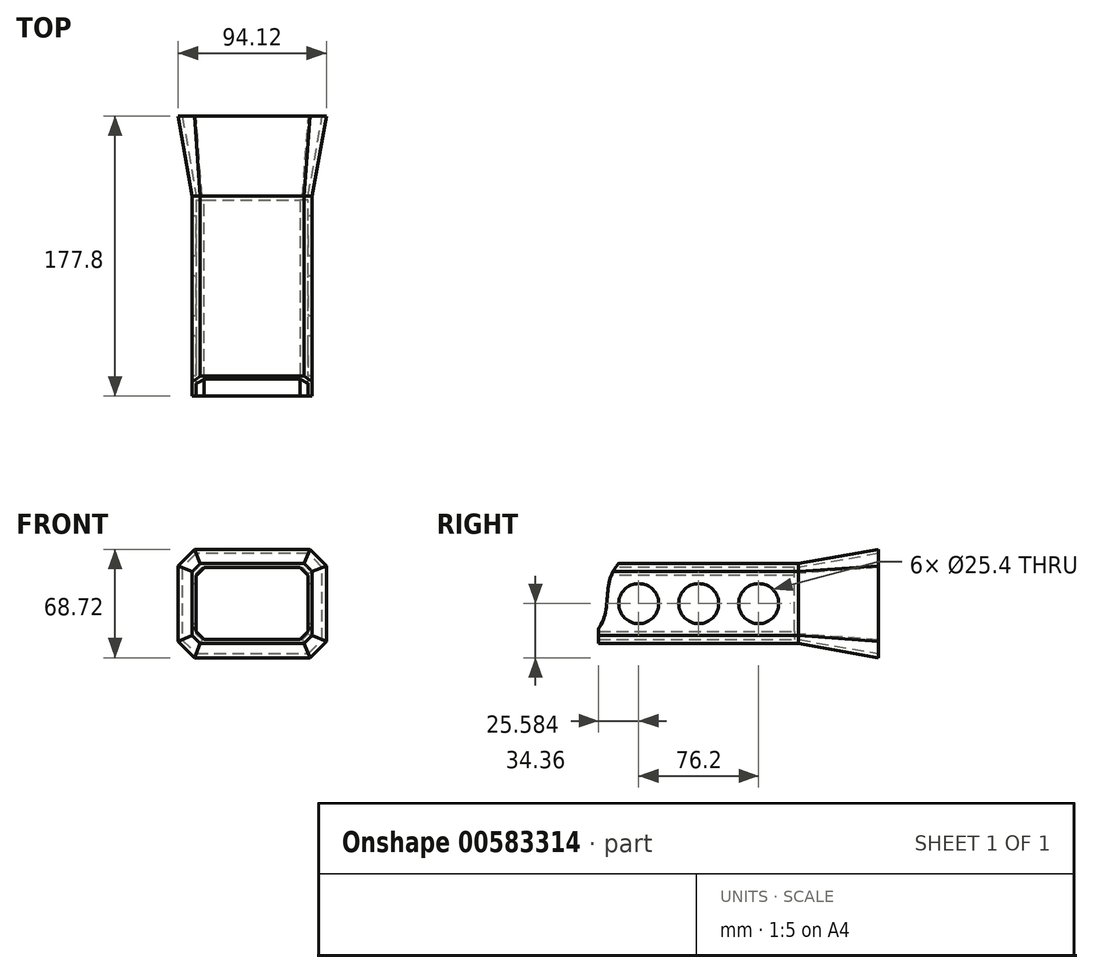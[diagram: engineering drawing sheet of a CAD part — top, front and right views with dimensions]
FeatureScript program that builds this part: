
annotation { "Feature Type Name" : "Feature", "Feature Type Description" : "" }
export const myFeature = defineFeature(function(context is Context, id is Id, definition is map)
    precondition{}
    {
        {
            var Q0;
            Q0=qCreatedBy(makeId("Front.planeOp"),FACE);
            var sketch = newSketch(context, id + "F0", { "sketchPlane" : qUnion([Q0])});
            skLineSegment(sketch, "E0.bottom", {"start": v(0, 0) * mm, "end": v(76.2, 0) * mm});
            skLineSegment(sketch, "E0.top", {"start": v(0, 50.8) * mm, "end": v(76.2, 50.8) * mm});
            skLineSegment(sketch, "E0.left", {"start": v(0, 0) * mm, "end": v(0, 50.8) * mm});
            skLineSegment(sketch, "E0.right", {"start": v(76.2, 0) * mm, "end": v(76.2, 50.8) * mm});
            skSolve(sketch);
        }
        {
            var Q0;
            Q0 = qSketchRegion(id + "F0", true);
            extrude(context, id + "F1", {"entities" : qUnion([Q0]), "depth" : 127 * mm, "offsetDistance" : 25.4 * mm});
        }
        {
            var Q0;
            Q0=makeQuery(id+"F1.opExtrude","CAP_FACE",FACE,{"disambiguationData":[OSD([sQuery(id+"F0.wireOp",EDGE,"E0.bottom"),sQuery(id+"F0.wireOp",EDGE,"E0.top"),sQuery(id+"F0.wireOp",EDGE,"E0.left"),sQuery(id+"F0.wireOp",EDGE,"E0.right")])],"isStart":false});
            shell(context, id + "F2", {"entities" : qUnion([Q0]), "thickness" : 2.54 * mm});
        }
        {
            var Q0;
            Q0=makeQuery(id+"F1.opExtrude","SWEPT_FACE",FACE,{"disambiguationData":[OSD([sQuery(id+"F0.wireOp",EDGE,"E0.right")])]});
            var sketch = newSketch(context, id + "F3", { "sketchPlane" : qUnion([Q0])});
            skCircle(sketch, "E1", {"center": v(-101.42, 25.4) * mm, "radius": 12.7 * mm});
            skCircle(sketch, "E2", {"center": v(-63.32, 25.4) * mm, "radius": 12.7 * mm});
            skCircle(sketch, "E3", {"center": v(-25.22, 25.4) * mm, "radius": 12.7 * mm});
            skSolve(sketch);
        }
        {
            var Q0;
            Q0=makeQuery(id+"F3.imprint","IMPRINT",FACE,{"disambiguationData":[TD([[makeQuery(id+"F3.imprint","IMPRINT",EDGE,{"derivedFrom":sQuery(id+"F3.wireOp",EDGE,"E1")}),1.0]])]});
            var Q1;
            Q1=makeQuery(id+"F3.imprint","IMPRINT",FACE,{"disambiguationData":[TD([[makeQuery(id+"F3.imprint","IMPRINT",EDGE,{"derivedFrom":sQuery(id+"F3.wireOp",EDGE,"E2")}),1.0]])]});
            var Q2;
            Q2=makeQuery(id+"F3.imprint","IMPRINT",FACE,{"disambiguationData":[TD([[makeQuery(id+"F3.imprint","IMPRINT",EDGE,{"derivedFrom":sQuery(id+"F3.wireOp",EDGE,"E3")}),1.0]])]});
            extrude(context, id + "F4", {"entities" : qUnion([Q0, Q1, Q2]), "operationType" : NewBodyOperationType.REMOVE, "endBound" : BoundingType.THROUGH_ALL, "oppositeDirection" : true, "depth" : 25.4 * mm, "offsetDistance" : 25.4 * mm});
        }
        {
            var Q0;
            Q0=makeQuery(id+"F1.opExtrude","SWEPT_FACE",FACE,{"disambiguationData":[OSD([sQuery(id+"F0.wireOp",EDGE,"E0.right")])]});
            var sketch = newSketch(context, id + "F5", { "sketchPlane" : qUnion([Q0])});
            skFitSpline(sketch, "E4", {"points": [v(-105.13, 60.93) * mm, v(-119.3, 42.33) * mm, v(-123.68, 15.71) * mm, v(-145.7, -4.89) * mm], "startDerivative": vector(-47.95, -55.16) * mm, "endDerivative": vector(-90.34, -45.67) * mm});
            skSolve(sketch);
        }
        {
            var Q0;
            Q0 = qSketchRegion(id + "F5", true);
            var Q1;
            {var subQ0=sQuery(id+"F5.wireOp",EDGE,"E4");var subQ1=sQuery(id+"F0.wireOp",EDGE,"E0.right");var subQ4=makeQuery(id+"F1.opExtrude","CAP_EDGE",EDGE,{"disambiguationData":[OSD([subQ1])],"isStart":false});var subQ5=makeQuery(id+"F5.imprint","INTERSECT",VERTEX,{"derivedFrom":[subQ4,subQ0]});Q1=makeQuery(id+"F5.imprint","IMPRINT",FACE,{"disambiguationData":[TD([[makeQuery(id+"F5.imprint","IMPRINT",EDGE,{"disambiguationData":[TD([[subQ5,1.0]])],"derivedFrom":subQ0}),-1.0]])]});}
            extrude(context, id + "F6", {"entities" : qUnion([Q0, Q1]), "operationType" : NewBodyOperationType.REMOVE, "endBound" : BoundingType.THROUGH_ALL, "oppositeDirection" : true, "depth" : 25.4 * mm, "offsetDistance" : 25.4 * mm});
        }
        {
            var Q0;
            Q0=makeQuery(id+"F2.opShell","OFFSET_EDGE",EDGE,{"disambiguationData":[OSD([sQuery(id+"F0.wireOp",EDGE,"E0.bottom"),sQuery(id+"F0.wireOp",EDGE,"E0.left")])]});
            var Q1;
            Q1=makeQuery(id+"F2.opShell","OFFSET_EDGE",EDGE,{"disambiguationData":[OSD([sQuery(id+"F0.wireOp",EDGE,"E0.bottom"),sQuery(id+"F0.wireOp",EDGE,"E0.right")])]});
            var Q2;
            Q2=makeQuery(id+"F2.opShell","OFFSET_EDGE",EDGE,{"disambiguationData":[OSD([sQuery(id+"F0.wireOp",EDGE,"E0.top"),sQuery(id+"F0.wireOp",EDGE,"E0.left")])]});
            var Q3;
            Q3=makeQuery(id+"F2.opShell","OFFSET_EDGE",EDGE,{"disambiguationData":[OSD([sQuery(id+"F0.wireOp",EDGE,"E0.top"),sQuery(id+"F0.wireOp",EDGE,"E0.right")])]});
            var Q4;
            Q4=makeQuery(id+"F1.opExtrude","SWEPT_EDGE",EDGE,{"disambiguationData":[OSD([sQuery(id+"F0.wireOp",EDGE,"E0.top"),sQuery(id+"F0.wireOp",EDGE,"E0.left")])]});
            var Q5;
            Q5=makeQuery(id+"F1.opExtrude","SWEPT_EDGE",EDGE,{"disambiguationData":[OSD([sQuery(id+"F0.wireOp",EDGE,"E0.top"),sQuery(id+"F0.wireOp",EDGE,"E0.right")])]});
            var Q6;
            Q6=makeQuery(id+"F1.opExtrude","SWEPT_EDGE",EDGE,{"disambiguationData":[OSD([sQuery(id+"F0.wireOp",EDGE,"E0.bottom"),sQuery(id+"F0.wireOp",EDGE,"E0.left")])]});
            var Q7;
            Q7=makeQuery(id+"F1.opExtrude","SWEPT_EDGE",EDGE,{"disambiguationData":[OSD([sQuery(id+"F0.wireOp",EDGE,"E0.bottom"),sQuery(id+"F0.wireOp",EDGE,"E0.right")])]});
            chamfer(context, id + "F7", {"entities" : qUnion([Q0, Q1, Q2, Q3, Q4, Q5, Q6, Q7]), "width" : 5.08 * mm, "tangentPropagation" : true});
        }
        {
            var Q0;
            Q0=makeQuery(id+"F1.opExtrude","CAP_FACE",FACE,{"disambiguationData":[OSD([sQuery(id+"F0.wireOp",EDGE,"E0.bottom"),sQuery(id+"F0.wireOp",EDGE,"E0.top"),sQuery(id+"F0.wireOp",EDGE,"E0.left"),sQuery(id+"F0.wireOp",EDGE,"E0.right")])],"isStart":true});
            var sketch = newSketch(context, id + "F8", { "sketchPlane" : qUnion([Q0])});
            skLineSegment(sketch, "E5.0", {"start": v(-5.08, 50.8) * mm, "end": v(-71.12, 50.8) * mm});
            skPoint(sketch, "E6.0", {"position": v(-73.66, 48.26) * mm});
            skLineSegment(sketch, "E7.0.0", {"start": v(-76.2, 9.5) * mm, "end": v(-76.2, 5.08) * mm});
            skLineSegment(sketch, "E7.0.2", {"start": v(-76.2, 5.08) * mm, "end": v(-76.2, 45.72) * mm});
            skFitSpline(sketch, "E7.0.4", {"points": [v(-76.2, 60.93) * mm, v(-76.2, 55.2) * mm, v(-76.2, 43.95) * mm, v(-76.2, 13.07) * mm, v(-76.2, 0.5) * mm, v(-76.2, -4.89) * mm]});
            skPoint(sketch, "E8.0", {"position": v(-73.66, 2.54) * mm});
            skLineSegment(sketch, "E9.0", {"start": v(-5.08, 0) * mm, "end": v(-71.12, 0) * mm});
            skLineSegment(sketch, "E10.0", {"start": v(-76.2, 5.08) * mm, "end": v(-71.12, 0) * mm});
            skLineSegment(sketch, "E11.0", {"start": v(0, 45.72) * mm, "end": v(-5.08, 50.8) * mm});
            skLineSegment(sketch, "E12.0", {"start": v(0, 5.08) * mm, "end": v(0, 45.72) * mm});
            skLineSegment(sketch, "E13.0", {"start": v(-5.08, 0) * mm, "end": v(0, 5.08) * mm});
            skSolve(sketch);
        }
        {
            var Q0;
            Q0=makeQuery(id+"F8.imprint","IMPRINT",FACE,{"disambiguationData":[TD([[makeQuery(id+"F8.imprint","IMPRINT",EDGE,{"derivedFrom":sQuery(id+"F8.wireOp",EDGE,"E5.0")}),1.0]])]});
            extrude(context, id + "F9", {"entities" : qUnion([Q0]), "operationType" : NewBodyOperationType.ADD, "depth" : 50.8 * mm, "offsetDistance" : 25.4 * mm, "hasDraft" : true, "draftAngle" : 10 * degree});
        }
        {
            var Q0;
            Q0=makeQuery(id+"F9.opExtrude","CAP_FACE",FACE,{"disambiguationData":[OSD([sQuery(id+"F0.wireOp",EDGE,"E0.bottom"),sQuery(id+"F0.wireOp",EDGE,"E0.top"),sQuery(id+"F0.wireOp",EDGE,"E0.left"),sQuery(id+"F0.wireOp",EDGE,"E0.right"),sQuery(id+"F8.wireOp",EDGE,"E5.0"),sQuery(id+"F8.wireOp",EDGE,"E7.0.2"),sQuery(id+"F8.wireOp",EDGE,"E7.0.4"),sQuery(id+"F8.wireOp",EDGE,"E9.0"),sQuery(id+"F8.wireOp",EDGE,"E10.0"),sQuery(id+"F8.wireOp",EDGE,"E11.0"),sQuery(id+"F8.wireOp",EDGE,"E12.0"),sQuery(id+"F8.wireOp",EDGE,"E13.0")])],"isStart":false});
            shell(context, id + "F10", {"entities" : qUnion([Q0]), "thickness" : 2.54 * mm});
        }
    });
